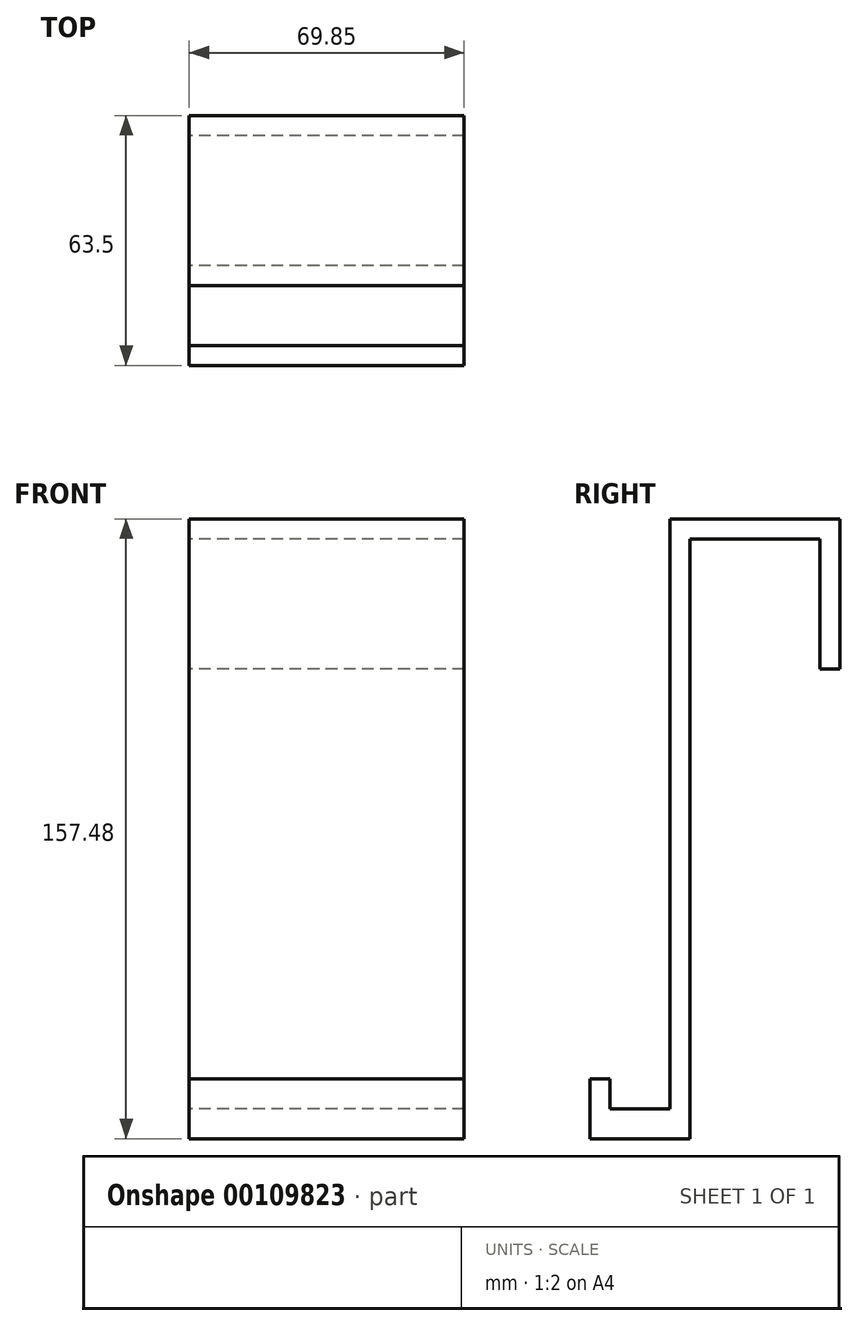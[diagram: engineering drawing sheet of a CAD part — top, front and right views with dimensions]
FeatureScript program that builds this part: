
annotation { "Feature Type Name" : "Feature", "Feature Type Description" : "" }
export const myFeature = defineFeature(function(context is Context, id is Id, definition is map)
    precondition{}
    {
        {
            var Q0;
            Q0=qCreatedBy(makeId("Right.planeOp"),FACE);
            var sketch = newSketch(context, id + "F0", { "sketchPlane" : qUnion([Q0])});
            skLineSegment(sketch, "E0", {"start": v(0, 0) * mm, "end": v(5.08, 0) * mm});
            skLineSegment(sketch, "E1", {"start": v(5.08, 0) * mm, "end": v(5.08, -7.62) * mm});
            skLineSegment(sketch, "E2", {"start": v(5.08, -7.62) * mm, "end": v(20.32, -7.62) * mm});
            skLineSegment(sketch, "E3", {"start": v(20.32, -7.62) * mm, "end": v(20.32, 142.24) * mm});
            skLineSegment(sketch, "E4", {"start": v(20.32, 142.24) * mm, "end": v(63.5, 142.24) * mm});
            skLineSegment(sketch, "E5", {"start": v(63.5, 142.24) * mm, "end": v(63.5, 104.14) * mm});
            skLineSegment(sketch, "E6", {"start": v(63.5, 104.14) * mm, "end": v(58.42, 104.14) * mm});
            skLineSegment(sketch, "E7", {"start": v(58.42, 104.14) * mm, "end": v(58.42, 137.16) * mm});
            skLineSegment(sketch, "E8", {"start": v(58.42, 137.16) * mm, "end": v(25.4, 137.16) * mm});
            skLineSegment(sketch, "E9", {"start": v(25.4, 137.16) * mm, "end": v(25.4, -15.24) * mm});
            skLineSegment(sketch, "E10", {"start": v(25.4, -15.24) * mm, "end": v(0, -15.24) * mm});
            skLineSegment(sketch, "E11", {"start": v(0, -15.24) * mm, "end": v(0, 0) * mm});
            skSolve(sketch);
        }
        {
            var Q0;
            Q0 = qSketchRegion(id + "F0", true);
            extrude(context, id + "F1", {"entities" : qUnion([Q0]), "depth" : 69.85 * mm});
        }
    });
